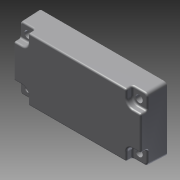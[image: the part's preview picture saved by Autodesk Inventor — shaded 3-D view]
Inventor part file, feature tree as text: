
AUTODESK INVENTOR PART (.ipt)
format: ipt  version: 2013 (Build 170138000, 138)  size: 472,576 bytes
history: native  units: in
note: dims shown in document units (in); Inventor stores cm internally (conversion verified against a paired STEP export)
features: sketch x16, extrude x13, mirror x6, fillet x3, plane x2, hole x1
ambient origin geometry x8: Origin, YZ Plane, XZ Plane, XY Plane, X Axis, Y Axis, Z Axis, Center Point
bodies: Solid1 (feature_tree)
feature tree (41):
  extrude  "Extrusion1"  Depth=0.059in TaperAngle=0.0deg
  extrude  "Extrusion2"  Depth=0.079in
  extrude  "Extrusion4"  Depth=0.081in TaperAngle=0.0deg
  extrude  "Extrusion5"  Depth=0.236in TaperAngle=0.0deg
  plane  "Work Plane1"
  plane  "Work Plane2"
  mirror  "Mirror1"
  mirror  "Mirror2"
  sketch  "Sketch5"  dims[d18=0.039in d19=0.0195in]
  extrude  "Extrusion6"  Depth=0.0195in
  mirror  "Mirror3"
  mirror  "Mirror4"
  extrude  "Extrusion7"  Depth=0.079in TaperAngle=0.0deg
  extrude  "Extrusion8"  Depth=0.079in TaperAngle=0.0deg
  extrude  "Extrusion9"  Depth=0.0344in
  extrude  "Extrusion10"  Depth=0.181in
  sketch  "Sketch11"  dims[d34=0.087in d35=0.75in d36=0.375in d37=0.25in d38=0.5635in d39=1.0in d40=0.8108in d41=0.079in d42=0.0103in]
  extrude  "Extrusion11"  Depth=0.142in TaperAngle=0.0deg
  extrude  "Extrusion12"  Depth=0.079in
  extrude  "Extrusion13"  Depth=0.02in
  hole  "Hole1"  [1 undecoded]
  extrude  "Extrusion14"  [1 undecoded]
  mirror  "Mirror5"
  mirror  "Mirror6"
  fillet  "Fillet1"  [1 undecoded]
  fillet  "Fillet2"  [1 undecoded]
  fillet  "Fillet3"  [1 undecoded]
  sketch  "Sketch1"  dims[d0=0.315in d1=-0.0103in d2=0.059in d3=0.0in]
  sketch  "Sketch2"  dims[d6=0.197in d7=-0.0103in d8=0.079in d9=0.0103in]
  sketch  "Sketch3"  dims[d10=0.1085in d11=0.0in d12=0.081in d13=0.0in]
  sketch  "Sketch4"  dims[d14=0.091in d15=0.0in d16=0.236in d17=0.0in]
  sketch  "Sketch6"  dims[d20=0.606in d21=0.079in d22=0.0in]
  sketch  "Sketch7"  dims[d23=0.606in d24=0.079in d25=0.0in]
  sketch  "Sketch8"  dims[d26=0.0344in d27=0.0344in]
  sketch  "Sketch9"  dims[d28=0.039in d29=0.0in d30=0.181in]
  sketch  "Sketch10"  dims[d31=0.0905in d32=0.142in d33=0.0in]
  sketch  "Sketch12"  dims[d43=0.02in d44=0.02in]
  sketch  "Sketch13"  dims[d45=0.0395in]
  sketch  "Sketch14"
  sketch  "Sketch16"
  sketch  "Sketch17"
note: 5 required parameter values undecoded (feature->parameter linkage not recoverable at this tier; creation-order binding heuristic only, values carry confidence <= 0.55)
